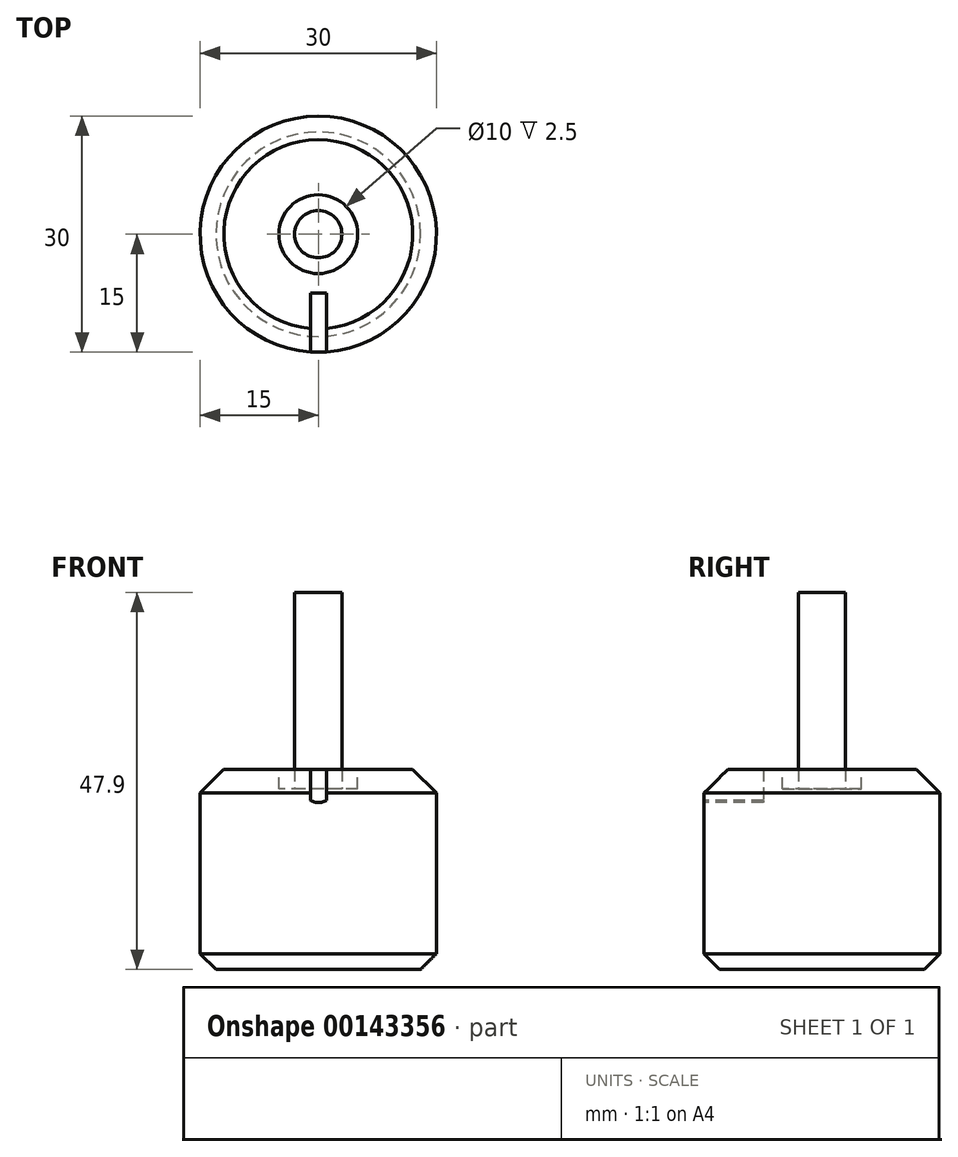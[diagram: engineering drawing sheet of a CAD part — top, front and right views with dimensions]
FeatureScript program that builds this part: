
annotation { "Feature Type Name" : "Feature", "Feature Type Description" : "" }
export const myFeature = defineFeature(function(context is Context, id is Id, definition is map)
    precondition{}
    {
        {
            var Q0;
            Q0=qCreatedBy(makeId("Top.planeOp"),FACE);
            var sketch = newSketch(context, id + "F0", { "sketchPlane" : qUnion([Q0])});
            skCircle(sketch, "E0", {"center": v(0, 0) * mm, "radius": 15 * mm});
            skSolve(sketch);
        }
        {
            var Q0;
            Q0=makeQuery(id+"F0.imprint","IMPRINT",FACE,{"disambiguationData":[TD([[makeQuery(id+"F0.imprint","IMPRINT",EDGE,{"derivedFrom":sQuery(id+"F0.wireOp",EDGE,"E0")}),1.0]])]});
            extrude(context, id + "F1", {"entities" : qUnion([Q0]), "depth" : 25.4 * mm});
        }
        {
            var Q0;
            Q0=makeQuery(id+"F1.opExtrude","CAP_EDGE",EDGE,{"disambiguationData":[OSD([sQuery(id+"F0.wireOp",EDGE,"E0")])],"isStart":false});
            chamfer(context, id + "F2", {"entities" : qUnion([Q0]), "width" : 3 * mm, "tangentPropagation" : true});
        }
        {
            var Q0;
            Q0=makeQuery(id+"F1.opExtrude","CAP_EDGE",EDGE,{"disambiguationData":[OSD([sQuery(id+"F0.wireOp",EDGE,"E0")])],"isStart":true});
            chamfer(context, id + "F3", {"entities" : qUnion([Q0]), "width" : 2 * mm, "tangentPropagation" : true});
        }
        {
            var Q0;
            Q0=makeQuery(id+"F1.opExtrude","CAP_FACE",FACE,{"disambiguationData":[OSD([sQuery(id+"F0.wireOp",EDGE,"E0")])],"isStart":false});
            var sketch = newSketch(context, id + "F4", { "sketchPlane" : qUnion([Q0])});
            skCircle(sketch, "E1", {"center": v(0, 0) * mm, "radius": 5 * mm});
            skSolve(sketch);
        }
        {
            var Q0;
            Q0=makeQuery(id+"F4.imprint","IMPRINT",FACE,{"disambiguationData":[TD([[makeQuery(id+"F4.imprint","IMPRINT",EDGE,{"derivedFrom":sQuery(id+"F4.wireOp",EDGE,"E1")}),1.0]])]});
            extrude(context, id + "F5", {"entities" : qUnion([Q0]), "operationType" : NewBodyOperationType.REMOVE, "oppositeDirection" : true, "depth" : 2.5 * mm});
        }
        {
            var Q0;
            Q0=makeQuery(id+"F5.boolean.opBoolean","COPY",FACE,{"derivedFrom":makeQuery(id+"F5.opExtrude","CAP_FACE",FACE,{"disambiguationData":[OSD([sQuery(id+"F4.wireOp",EDGE,"E1")])],"isStart":false})});
            var sketch = newSketch(context, id + "F6", { "sketchPlane" : qUnion([Q0])});
            skCircle(sketch, "E2", {"center": v(0, 0) * mm, "radius": 3 * mm});
            skSolve(sketch);
        }
        {
            var Q0;
            Q0=makeQuery(id+"F6.imprint","IMPRINT",FACE,{"disambiguationData":[TD([[makeQuery(id+"F6.imprint","IMPRINT",EDGE,{"derivedFrom":sQuery(id+"F6.wireOp",EDGE,"E2")}),1.0]])]});
            extrude(context, id + "F7", {"entities" : qUnion([Q0]), "operationType" : NewBodyOperationType.ADD, "depth" : 25 * mm});
        }
        {
            var Q0;
            Q0=qCreatedBy(makeId("Front.planeOp"),FACE);
            cPlane(context, id + "F8", {"entities" : qUnion([Q0]), "cplaneType" : CPlaneType.OFFSET, "offset" : 15 * mm, "width" : 150 * mm, "height" : 150 * mm});
        }
        {
            var Q0;
            Q0=qCreatedBy(id+"F8.planeOp",FACE);
            var sketch = newSketch(context, id + "F9", { "sketchPlane" : qUnion([Q0])});
            skLineSegment(sketch, "E3.bottom", {"start": v(-0.98, 25.46) * mm, "end": v(1.02, 25.46) * mm});
            skLineSegment(sketch, "E3.left", {"start": v(-0.98, 25.46) * mm, "end": v(-0.98, 21.46) * mm});
            skLineSegment(sketch, "E3.right", {"start": v(1.02, 25.46) * mm, "end": v(1.02, 21.46) * mm});
            skArc(sketch, "E4", {"start": v(-0.98, 21.46) * mm, "mid": v(0.02, 21.2) * mm, "end": v(1.02, 21.46) * mm});
            skSolve(sketch);
        }
        {
            var Q0;
            Q0=makeQuery(id+"F9.imprint","IMPRINT",FACE,{"disambiguationData":[TD([[makeQuery(id+"F9.imprint","IMPRINT",EDGE,{"derivedFrom":sQuery(id+"F9.wireOp",EDGE,"E3.bottom")}),-1.0]])]});
            extrude(context, id + "F10", {"entities" : qUnion([Q0]), "operationType" : NewBodyOperationType.REMOVE, "oppositeDirection" : true, "depth" : 7.54 * mm});
        }
    });
